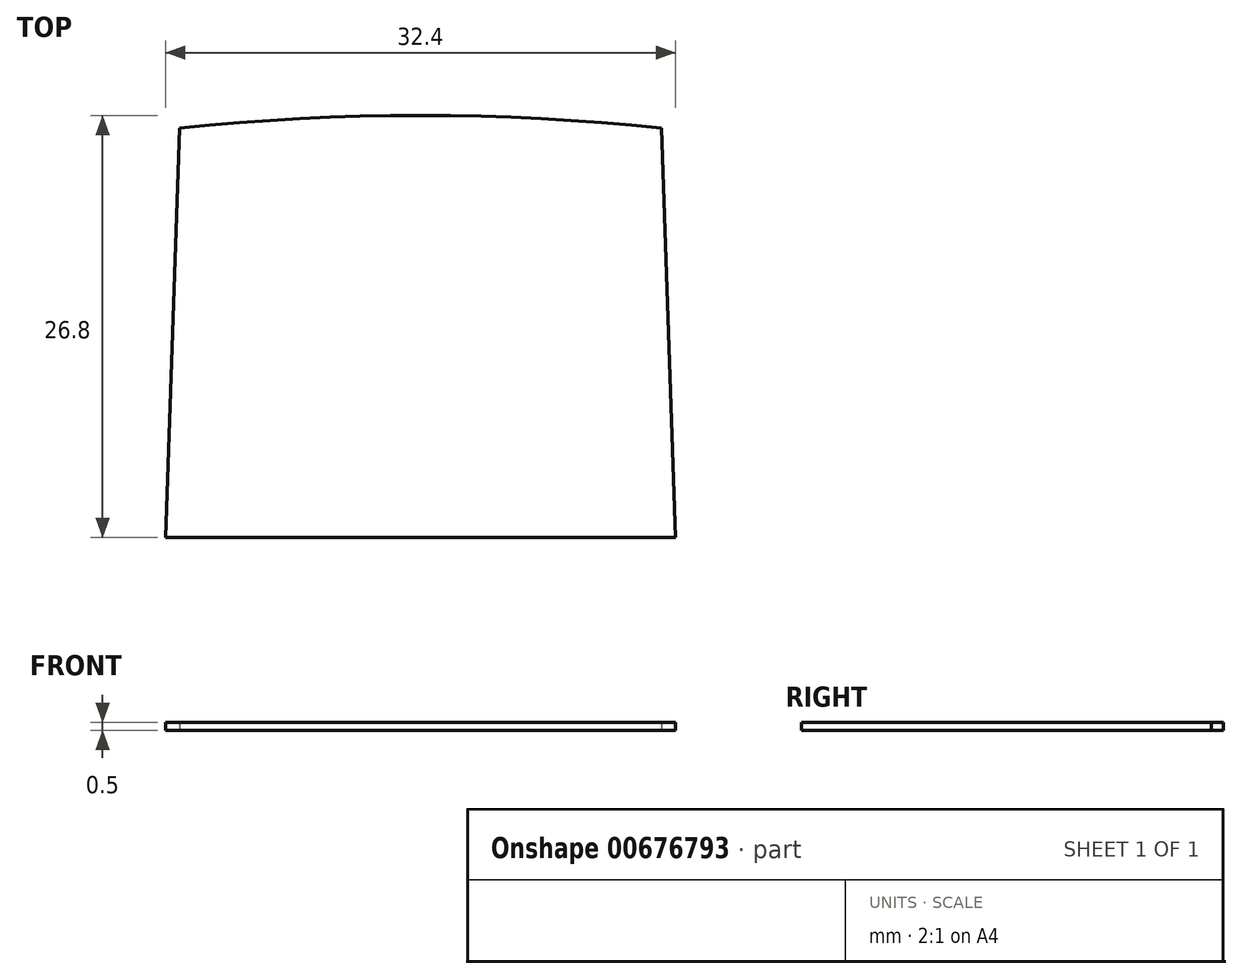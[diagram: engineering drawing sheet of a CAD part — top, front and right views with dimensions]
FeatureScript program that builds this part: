
annotation { "Feature Type Name" : "Feature", "Feature Type Description" : "" }
export const myFeature = defineFeature(function(context is Context, id is Id, definition is map)
    precondition{}
    {
        {
            var Q0;
            Q0=qCreatedBy(makeId("Top.planeOp"),FACE);
            var sketch = newSketch(context, id + "F0", { "sketchPlane" : qUnion([Q0])});
            skLineSegment(sketch, "E0", {"start": v(-25, 0) * mm, "end": v(-16.2, 0) * mm, "construction": true});
            skLineSegment(sketch, "E1", {"start": v(25, 0) * mm, "end": v(25, 24.7) * mm, "construction": true});
            skLineSegment(sketch, "E2", {"start": v(-25, 0) * mm, "end": v(-25, 24.7) * mm, "construction": true});
            skArc(sketch, "E3", {"start": v(-25, 24.7) * mm, "mid": v(-20.16, 25.44) * mm, "end": v(-15.3, 26.02) * mm, "construction": true});
            skPoint(sketch, "E4", {"position": v(0, 26.8) * mm});
            skLineSegment(sketch, "E5", {"start": v(15.3, 26.02) * mm, "end": v(16.2, 0) * mm});
            skLineSegment(sketch, "E6", {"start": v(-15.3, 26.02) * mm, "end": v(-16.2, 0) * mm});
            skArc(sketch, "E7", {"start": v(-15.3, 26.02) * mm, "mid": v(0, 26.8) * mm, "end": v(15.3, 26.02) * mm});
            skLineSegment(sketch, "E8", {"start": v(-16.2, 0) * mm, "end": v(16.2, 0) * mm});
            skLineSegment(sketch, "E9", {"start": v(16.2, 0) * mm, "end": v(25, 0) * mm, "construction": true});
            skArc(sketch, "E10", {"start": v(15.3, 26.02) * mm, "mid": v(20.16, 25.44) * mm, "end": v(25, 24.7) * mm, "construction": true});
            skSolve(sketch);
        }
        {
            var Q0;
            Q0 = qSketchRegion(id + "F0", true);
            extrude(context, id + "F1", {"entities" : qUnion([Q0]), "depth" : 0.5 * mm, "offsetDistance" : 25 * mm});
        }
    });
